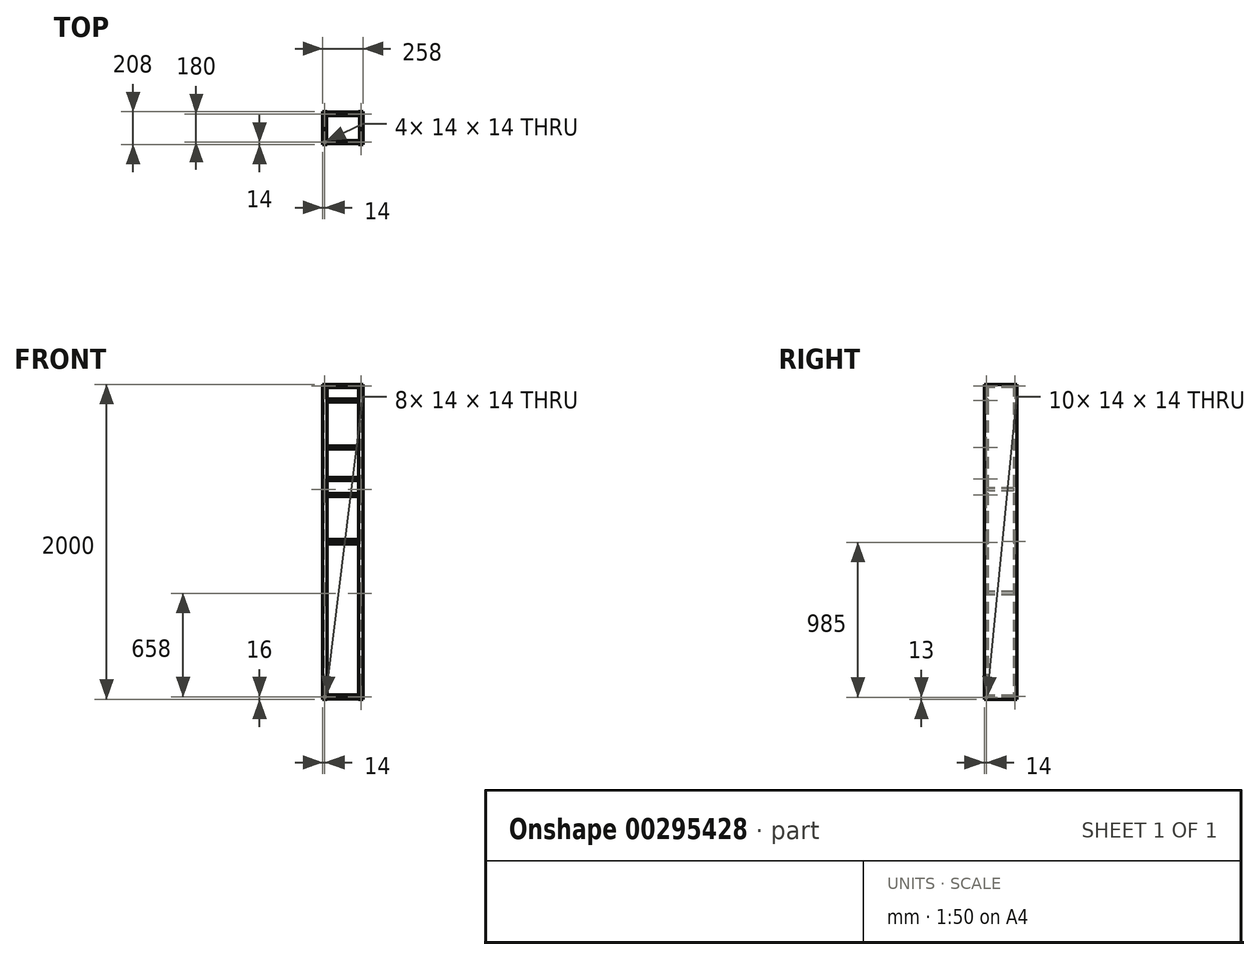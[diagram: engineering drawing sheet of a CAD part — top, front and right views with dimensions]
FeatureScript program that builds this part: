
annotation { "Feature Type Name" : "Feature", "Feature Type Description" : "" }
export const myFeature = defineFeature(function(context is Context, id is Id, definition is map)
    precondition{}
    {
        {
            var Q0;
            Q0=qCreatedBy(makeId("Top.planeOp"),FACE);
            var sketch = newSketch(context, id + "F0", { "sketchPlane" : qUnion([Q0])});
            skLineSegment(sketch, "E0", {"start": v(125, 0) * mm, "end": v(125, 100) * mm, "construction": true});
            skLineSegment(sketch, "E1", {"start": v(125, 100) * mm, "end": v(0, 100) * mm, "construction": true});
            skLineSegment(sketch, "E2.bottom", {"start": v(0, 0) * mm, "end": v(20, 0) * mm});
            skLineSegment(sketch, "E2.top", {"start": v(0, 20) * mm, "end": v(20, 20) * mm});
            skLineSegment(sketch, "E2.left", {"start": v(0, 0) * mm, "end": v(0, 20) * mm});
            skLineSegment(sketch, "E2.right", {"start": v(20, 0) * mm, "end": v(20, 20) * mm});
            skLineSegment(sketch, "E3.0", {"start": v(3, 17) * mm, "end": v(17, 17) * mm});
            skLineSegment(sketch, "E3.1", {"start": v(3, 3) * mm, "end": v(3, 17) * mm});
            skLineSegment(sketch, "E3.2", {"start": v(3, 3) * mm, "end": v(17, 3) * mm});
            skLineSegment(sketch, "E3.3", {"start": v(17, 3) * mm, "end": v(17, 17) * mm});
            skLineSegment(sketch, "E4.MirrorCS", {"start": v(250, 0) * mm, "end": v(230, 0) * mm});
            skLineSegment(sketch, "E5.MirrorCS", {"start": v(250, 20) * mm, "end": v(230, 20) * mm});
            skLineSegment(sketch, "E6.MirrorCS", {"start": v(250, 0) * mm, "end": v(250, 20) * mm});
            skLineSegment(sketch, "E7.MirrorCS", {"start": v(233, 3) * mm, "end": v(233, 17) * mm});
            skLineSegment(sketch, "E8.MirrorCS", {"start": v(247, 3) * mm, "end": v(233, 3) * mm});
            skLineSegment(sketch, "E9.MirrorCS", {"start": v(230, 0) * mm, "end": v(230, 20) * mm});
            skLineSegment(sketch, "E10.MirrorCS", {"start": v(247, 17) * mm, "end": v(233, 17) * mm});
            skLineSegment(sketch, "E11.MirrorCS", {"start": v(247, 3) * mm, "end": v(247, 17) * mm});
            skLineSegment(sketch, "E12.MirrorCS", {"start": v(247, 183) * mm, "end": v(233, 183) * mm});
            skLineSegment(sketch, "E13.MirrorCS", {"start": v(250, 200) * mm, "end": v(250, 180) * mm});
            skLineSegment(sketch, "E14.MirrorCS", {"start": v(250, 180) * mm, "end": v(230, 180) * mm});
            skLineSegment(sketch, "E15.MirrorCS", {"start": v(250, 200) * mm, "end": v(230, 200) * mm});
            skLineSegment(sketch, "E16.MirrorCS", {"start": v(17, 197) * mm, "end": v(17, 183) * mm});
            skLineSegment(sketch, "E17.MirrorCS", {"start": v(3, 197) * mm, "end": v(17, 197) * mm});
            skLineSegment(sketch, "E18.MirrorCS", {"start": v(3, 197) * mm, "end": v(3, 183) * mm});
            skLineSegment(sketch, "E19.MirrorCS", {"start": v(3, 183) * mm, "end": v(17, 183) * mm});
            skLineSegment(sketch, "E20.MirrorCS", {"start": v(20, 200) * mm, "end": v(20, 180) * mm});
            skLineSegment(sketch, "E21.MirrorCS", {"start": v(0, 200) * mm, "end": v(20, 200) * mm});
            skLineSegment(sketch, "E22.MirrorCS", {"start": v(0, 200) * mm, "end": v(0, 180) * mm});
            skLineSegment(sketch, "E23.MirrorCS", {"start": v(230, 200) * mm, "end": v(230, 180) * mm});
            skLineSegment(sketch, "E24.MirrorCS", {"start": v(0, 180) * mm, "end": v(20, 180) * mm});
            skLineSegment(sketch, "E25.MirrorCS", {"start": v(247, 197) * mm, "end": v(247, 183) * mm});
            skLineSegment(sketch, "E26.MirrorCS", {"start": v(247, 197) * mm, "end": v(233, 197) * mm});
            skLineSegment(sketch, "E27.MirrorCS", {"start": v(233, 197) * mm, "end": v(233, 183) * mm});
            skSolve(sketch);
        }
        {
            var Q0;
            Q0=makeQuery(id+"F0.imprint","IMPRINT",FACE,{"disambiguationData":[TD([[makeQuery(id+"F0.imprint","IMPRINT",EDGE,{"derivedFrom":sQuery(id+"F0.wireOp",EDGE,"E16.MirrorCS")}),1.0]])]});
            var Q1;
            Q1=makeQuery(id+"F0.imprint","IMPRINT",FACE,{"disambiguationData":[TD([[makeQuery(id+"F0.imprint","IMPRINT",EDGE,{"derivedFrom":sQuery(id+"F0.wireOp",EDGE,"E12.MirrorCS")}),1.0]])]});
            var Q2;
            Q2=makeQuery(id+"F0.imprint","IMPRINT",FACE,{"disambiguationData":[TD([[makeQuery(id+"F0.imprint","IMPRINT",EDGE,{"derivedFrom":sQuery(id+"F0.wireOp",EDGE,"E4.MirrorCS")}),-1.0]])]});
            var Q3;
            Q3=makeQuery(id+"F0.imprint","IMPRINT",FACE,{"disambiguationData":[TD([[makeQuery(id+"F0.imprint","IMPRINT",EDGE,{"derivedFrom":sQuery(id+"F0.wireOp",EDGE,"E2.bottom")}),1.0]])]});
            var Q4;
            Q4=makeQuery(id+"F0.imprint","IMPRINT",FACE,{"disambiguationData":[TD([[makeQuery(id+"F0.imprint","IMPRINT",EDGE,{"derivedFrom":sQuery(id+"F0.wireOp",EDGE,"1bdd15c0-c4f6-4624-8977-0df94d45482211.MirrorCS")}),1.0]])]});
            var Q5;
            Q5=makeQuery(id+"F0.imprint","IMPRINT",FACE,{"disambiguationData":[TD([[makeQuery(id+"F0.imprint","IMPRINT",EDGE,{"derivedFrom":sQuery(id+"F0.wireOp",EDGE,"1bdd15c0-c4f6-4624-8977-0df94d4548226.MirrorCS")}),-1.0]])]});
            extrude(context, id + "F1", {"entities" : qUnion([Q0, Q1, Q2, Q3, Q4, Q5]), "depth" : 2000 * mm});
        }
        {
            var Q0;
            Q0=qCreatedBy(makeId("Top.planeOp"),FACE);
            var sketch = newSketch(context, id + "F2", { "sketchPlane" : qUnion([Q0])});
            skLineSegment(sketch, "E28", {"start": v(0, 0) * mm, "end": v(0, 200.03) * mm});
            skLineSegment(sketch, "E29", {"start": v(125, 0) * mm, "end": v(125, 89.21) * mm, "construction": true});
            skLineSegment(sketch, "E30", {"start": v(0, 0) * mm, "end": v(20, 0) * mm});
            skLineSegment(sketch, "E31", {"start": v(20, 0) * mm, "end": v(20, 20) * mm});
            skLineSegment(sketch, "E32.0", {"start": v(24, -4) * mm, "end": v(24, 20) * mm});
            skLineSegment(sketch, "E32.2", {"start": v(-4, 204) * mm, "end": v(24, 204) * mm});
            skLineSegment(sketch, "E32.3", {"start": v(-4, -4) * mm, "end": v(-4, 204) * mm});
            skLineSegment(sketch, "E32.4", {"start": v(-4, -4) * mm, "end": v(24, -4) * mm});
            skLineSegment(sketch, "E33", {"start": v(24, 20) * mm, "end": v(20, 20) * mm});
            skLineSegment(sketch, "E34.MirrorCS", {"start": v(226, 20) * mm, "end": v(230, 20) * mm});
            skLineSegment(sketch, "E35.MirrorCS", {"start": v(250, 0) * mm, "end": v(250, 200) * mm});
            skLineSegment(sketch, "E36.MirrorCS", {"start": v(254, -4) * mm, "end": v(226, -4) * mm});
            skLineSegment(sketch, "E37.MirrorCS", {"start": v(254, 204) * mm, "end": v(226, 204) * mm});
            skLineSegment(sketch, "E38.MirrorCS", {"start": v(226, -4) * mm, "end": v(226, 20) * mm});
            skLineSegment(sketch, "E39.MirrorCS", {"start": v(230, 0) * mm, "end": v(230, 20) * mm});
            skLineSegment(sketch, "E40.MirrorCS", {"start": v(254, -4) * mm, "end": v(254, 204) * mm});
            skLineSegment(sketch, "E41.MirrorCS", {"start": v(250, 0) * mm, "end": v(230, 0) * mm});
            skLineSegment(sketch, "E42", {"start": v(0, 200.03) * mm, "end": v(20.11, 200.03) * mm});
            skLineSegment(sketch, "E43", {"start": v(20.11, 200.03) * mm, "end": v(20.11, 179.96) * mm});
            skLineSegment(sketch, "E44", {"start": v(20.11, 179.96) * mm, "end": v(24.11, 179.96) * mm});
            skLineSegment(sketch, "E45", {"start": v(24, 204) * mm, "end": v(24.11, 179.96) * mm});
            skLineSegment(sketch, "E46", {"start": v(249.91, 204) * mm, "end": v(226, 204) * mm});
            skLineSegment(sketch, "E47", {"start": v(250, 200) * mm, "end": v(230, 200) * mm});
            skLineSegment(sketch, "E48", {"start": v(230, 179.84) * mm, "end": v(230, 200) * mm});
            skLineSegment(sketch, "E49", {"start": v(230, 179.84) * mm, "end": v(226, 179.84) * mm});
            skLineSegment(sketch, "E50", {"start": v(226, 204) * mm, "end": v(226, 179.84) * mm});
            skSolve(sketch);
        }
        {
            var Q0;
            Q0 = qSketchRegion(id + "F2", true);
            extrude(context, id + "F3", {"entities" : qUnion([Q0]), "depth" : 2000 * mm});
        }
        {
            var Q0;
            Q0=makeQuery(id+"F1.opExtrude","SWEPT_FACE",FACE,{"disambiguationData":[OSD([sQuery(id+"F0.wireOp",EDGE,"E2.right")])]});
            var sketch = newSketch(context, id + "F4", { "sketchPlane" : qUnion([Q0])});
            skLineSegment(sketch, "E51.bottom", {"start": v(20, 2000) * mm, "end": v(0, 2000) * mm});
            skLineSegment(sketch, "E51.top", {"start": v(20, 1980) * mm, "end": v(0, 1980) * mm});
            skLineSegment(sketch, "E51.left", {"start": v(20, 2000) * mm, "end": v(20, 1980) * mm});
            skLineSegment(sketch, "E51.right", {"start": v(0, 2000) * mm, "end": v(0, 1980) * mm});
            skLineSegment(sketch, "E52.0", {"start": v(17, 1983) * mm, "end": v(3, 1983) * mm});
            skLineSegment(sketch, "E52.1", {"start": v(17, 1997) * mm, "end": v(17, 1983) * mm});
            skLineSegment(sketch, "E52.2", {"start": v(17, 1997) * mm, "end": v(3, 1997) * mm});
            skLineSegment(sketch, "E52.3", {"start": v(3, 1997) * mm, "end": v(3, 1983) * mm});
            skLineSegment(sketch, "E53.0.1.1", {"start": v(0, 1909) * mm, "end": v(0, 1889) * mm});
            skLineSegment(sketch, "E53.0.1.2", {"start": v(17, 1906) * mm, "end": v(3, 1906) * mm});
            skLineSegment(sketch, "E53.0.1.4", {"start": v(20, 1909) * mm, "end": v(0, 1909) * mm});
            skLineSegment(sketch, "E53.0.1.5", {"start": v(17, 1892) * mm, "end": v(3, 1892) * mm});
            skLineSegment(sketch, "E53.0.1.6", {"start": v(17, 1906) * mm, "end": v(17, 1892) * mm});
            skLineSegment(sketch, "E53.0.1.7", {"start": v(3, 1906) * mm, "end": v(3, 1892) * mm});
            skLineSegment(sketch, "E53.0.1.8", {"start": v(20, 1909) * mm, "end": v(20, 1889) * mm});
            skLineSegment(sketch, "E53.0.1.9", {"start": v(20, 1889) * mm, "end": v(0, 1889) * mm});
            skLineSegment(sketch, "E54.0.1.0", {"start": v(20, 1609) * mm, "end": v(20, 1589) * mm});
            skLineSegment(sketch, "E54.0.1.1", {"start": v(17, 1606) * mm, "end": v(3, 1606) * mm});
            skLineSegment(sketch, "E54.0.1.2", {"start": v(20, 1589) * mm, "end": v(0, 1589) * mm});
            skLineSegment(sketch, "E54.0.1.3", {"start": v(17, 1606) * mm, "end": v(17, 1592) * mm});
            skLineSegment(sketch, "E54.0.1.4", {"start": v(0, 1609) * mm, "end": v(0, 1589) * mm});
            skLineSegment(sketch, "E54.0.1.5", {"start": v(17, 1592) * mm, "end": v(3, 1592) * mm});
            skLineSegment(sketch, "E54.0.1.6", {"start": v(3, 1606) * mm, "end": v(3, 1592) * mm});
            skLineSegment(sketch, "E54.0.1.7", {"start": v(20, 1609) * mm, "end": v(0, 1609) * mm});
            skLineSegment(sketch, "E55.0.1.0", {"start": v(20, 1409) * mm, "end": v(20, 1389) * mm});
            skLineSegment(sketch, "E55.0.1.1", {"start": v(3, 1406) * mm, "end": v(3, 1392) * mm});
            skLineSegment(sketch, "E55.0.1.2", {"start": v(17, 1406) * mm, "end": v(17, 1392) * mm});
            skLineSegment(sketch, "E55.0.1.3", {"start": v(0, 1409) * mm, "end": v(0, 1389) * mm});
            skLineSegment(sketch, "E55.0.1.4", {"start": v(20, 1409) * mm, "end": v(0, 1409) * mm});
            skLineSegment(sketch, "E55.0.1.5", {"start": v(20, 1389) * mm, "end": v(0, 1389) * mm});
            skLineSegment(sketch, "E55.0.1.6", {"start": v(17, 1406) * mm, "end": v(3, 1406) * mm});
            skLineSegment(sketch, "E55.0.1.7", {"start": v(17, 1392) * mm, "end": v(3, 1392) * mm});
            skLineSegment(sketch, "E56.0.1.0", {"start": v(17, 1305) * mm, "end": v(17, 1291) * mm});
            skLineSegment(sketch, "E56.0.1.1", {"start": v(20, 1308) * mm, "end": v(0, 1308) * mm});
            skLineSegment(sketch, "E56.0.1.2", {"start": v(3, 1305) * mm, "end": v(3, 1291) * mm});
            skLineSegment(sketch, "E56.0.1.3", {"start": v(20, 1308) * mm, "end": v(20, 1288) * mm});
            skLineSegment(sketch, "E56.0.1.4", {"start": v(20, 1288) * mm, "end": v(0, 1288) * mm});
            skLineSegment(sketch, "E56.0.1.5", {"start": v(0, 1308) * mm, "end": v(0, 1288) * mm});
            skLineSegment(sketch, "E56.0.1.6", {"start": v(17, 1291) * mm, "end": v(3, 1291) * mm});
            skLineSegment(sketch, "E56.0.1.7", {"start": v(17, 1305) * mm, "end": v(3, 1305) * mm});
            skLineSegment(sketch, "E57.0.1.0", {"start": v(20, 1008) * mm, "end": v(20, 988) * mm});
            skLineSegment(sketch, "E57.0.1.1", {"start": v(0, 1008) * mm, "end": v(0, 988) * mm});
            skLineSegment(sketch, "E57.0.1.2", {"start": v(20, 988) * mm, "end": v(0, 988) * mm});
            skLineSegment(sketch, "E57.0.1.3", {"start": v(3, 1005) * mm, "end": v(3, 991) * mm});
            skLineSegment(sketch, "E57.0.1.4", {"start": v(20, 1008) * mm, "end": v(0, 1008) * mm});
            skLineSegment(sketch, "E57.0.1.5", {"start": v(17, 1005) * mm, "end": v(17, 991) * mm});
            skLineSegment(sketch, "E57.0.1.6", {"start": v(17, 991) * mm, "end": v(3, 991) * mm});
            skLineSegment(sketch, "E57.0.1.7", {"start": v(17, 1005) * mm, "end": v(3, 1005) * mm});
            skLineSegment(sketch, "E58.0.1.0", {"start": v(17, 20) * mm, "end": v(17, 6) * mm});
            skLineSegment(sketch, "E58.0.1.1", {"start": v(3, 20) * mm, "end": v(3, 6) * mm});
            skLineSegment(sketch, "E58.0.1.2", {"start": v(17, 6) * mm, "end": v(3, 6) * mm});
            skLineSegment(sketch, "E58.0.1.3", {"start": v(0, 23) * mm, "end": v(0, 3) * mm});
            skLineSegment(sketch, "E58.0.1.4", {"start": v(20, 3) * mm, "end": v(0, 3) * mm});
            skLineSegment(sketch, "E58.0.1.5", {"start": v(20, 23) * mm, "end": v(20, 3) * mm});
            skLineSegment(sketch, "E58.0.1.6", {"start": v(20, 23) * mm, "end": v(0, 23) * mm});
            skLineSegment(sketch, "E58.0.1.7", {"start": v(17, 20) * mm, "end": v(3, 20) * mm});
            skSolve(sketch);
        }
        {
            var Q0;
            Q0 = qSketchRegion(id + "F4", true);
            extrude(context, id + "F5", {"entities" : qUnion([Q0]), "depth" : 210 * mm});
        }
        {
            var Q0;
            Q0=makeQuery(id+"F1.opExtrude","SWEPT_FACE",FACE,{"disambiguationData":[OSD([sQuery(id+"F0.wireOp",EDGE,"E2.top")])]});
            var sketch = newSketch(context, id + "F6", { "sketchPlane" : qUnion([Q0])});
            skLineSegment(sketch, "E59.bottom", {"start": v(-20, 2000) * mm, "end": v(0, 2000) * mm});
            skLineSegment(sketch, "E59.top", {"start": v(-20, 1980) * mm, "end": v(0, 1980) * mm});
            skLineSegment(sketch, "E59.left", {"start": v(-20, 2000) * mm, "end": v(-20, 1980) * mm});
            skLineSegment(sketch, "E59.right", {"start": v(0, 2000) * mm, "end": v(0, 1980) * mm});
            skLineSegment(sketch, "E60.0", {"start": v(-17, 1997) * mm, "end": v(-17, 1983) * mm});
            skLineSegment(sketch, "E60.1", {"start": v(-17, 1997) * mm, "end": v(-3, 1997) * mm});
            skLineSegment(sketch, "E60.2", {"start": v(-3, 1997) * mm, "end": v(-3, 1983) * mm});
            skLineSegment(sketch, "E60.3", {"start": v(-17, 1983) * mm, "end": v(-3, 1983) * mm});
            skPoint(sketch, "E61.endSnap0", {"position": v(-17, 1990) * mm});
            skLineSegment(sketch, "E62.MirrorCS", {"start": v(-250, 2000) * mm, "end": v(-250, 1980) * mm});
            skLineSegment(sketch, "E63.MirrorCS", {"start": v(-233, 1997) * mm, "end": v(-233, 1983) * mm});
            skLineSegment(sketch, "E64.MirrorCS", {"start": v(-230, 1980) * mm, "end": v(-250, 1980) * mm});
            skLineSegment(sketch, "E65.MirrorCS", {"start": v(-233, 1983) * mm, "end": v(-247, 1983) * mm});
            skLineSegment(sketch, "E66.MirrorCS", {"start": v(-230, 2000) * mm, "end": v(-250, 2000) * mm});
            skPoint(sketch, "E67.MirrorP", {"position": v(-233, 1990) * mm});
            skLineSegment(sketch, "E68.MirrorCS", {"start": v(-233, 1997) * mm, "end": v(-247, 1997) * mm});
            skLineSegment(sketch, "E69.MirrorCS", {"start": v(-247, 1997) * mm, "end": v(-247, 1983) * mm});
            skLineSegment(sketch, "E70.MirrorCS", {"start": v(-230, 2000) * mm, "end": v(-230, 1980) * mm});
            skPoint(sketch, "E71.0.1.0", {"position": v(-17, 1332) * mm});
            skPoint(sketch, "E71.0.1.1", {"position": v(-233, 1332) * mm});
            skLineSegment(sketch, "E71.0.1.2", {"start": v(0, 1342) * mm, "end": v(0, 1322) * mm});
            skLineSegment(sketch, "E71.0.1.3", {"start": v(-17, 1339) * mm, "end": v(-17, 1325) * mm});
            skLineSegment(sketch, "E71.0.1.4", {"start": v(-20, 1322) * mm, "end": v(0, 1322) * mm});
            skLineSegment(sketch, "E71.0.1.5", {"start": v(-230, 1322) * mm, "end": v(-250, 1322) * mm});
            skLineSegment(sketch, "E71.0.1.6", {"start": v(-233, 1325) * mm, "end": v(-247, 1325) * mm});
            skLineSegment(sketch, "E71.0.1.7", {"start": v(-250, 1342) * mm, "end": v(-250, 1322) * mm});
            skLineSegment(sketch, "E71.0.1.8", {"start": v(-230, 1342) * mm, "end": v(-250, 1342) * mm});
            skLineSegment(sketch, "E71.0.1.9", {"start": v(-17, 1325) * mm, "end": v(-3, 1325) * mm});
            skLineSegment(sketch, "E71.0.1.10", {"start": v(-233, 1339) * mm, "end": v(-233, 1325) * mm});
            skLineSegment(sketch, "E71.0.1.11", {"start": v(-3, 1339) * mm, "end": v(-3, 1325) * mm});
            skLineSegment(sketch, "E71.0.1.12", {"start": v(-17, 1339) * mm, "end": v(-3, 1339) * mm});
            skLineSegment(sketch, "E71.0.1.13", {"start": v(-20, 1342) * mm, "end": v(-20, 1322) * mm});
            skLineSegment(sketch, "E71.0.1.14", {"start": v(-20, 1342) * mm, "end": v(0, 1342) * mm});
            skLineSegment(sketch, "E71.0.1.15", {"start": v(-230, 1342) * mm, "end": v(-230, 1322) * mm});
            skLineSegment(sketch, "E71.0.1.16", {"start": v(-247, 1339) * mm, "end": v(-247, 1325) * mm});
            skLineSegment(sketch, "E71.0.1.17", {"start": v(-233, 1339) * mm, "end": v(-247, 1339) * mm});
            skPoint(sketch, "E71.0.2.0", {"position": v(-17, 674) * mm});
            skPoint(sketch, "E71.0.2.1", {"position": v(-233, 674) * mm});
            skLineSegment(sketch, "E71.0.2.2", {"start": v(0, 684) * mm, "end": v(0, 664) * mm});
            skLineSegment(sketch, "E71.0.2.3", {"start": v(-17, 681) * mm, "end": v(-17, 667) * mm});
            skLineSegment(sketch, "E71.0.2.4", {"start": v(-20, 664) * mm, "end": v(0, 664) * mm});
            skLineSegment(sketch, "E71.0.2.5", {"start": v(-230, 664) * mm, "end": v(-250, 664) * mm});
            skLineSegment(sketch, "E71.0.2.6", {"start": v(-233, 667) * mm, "end": v(-247, 667) * mm});
            skLineSegment(sketch, "E71.0.2.7", {"start": v(-250, 684) * mm, "end": v(-250, 664) * mm});
            skLineSegment(sketch, "E71.0.2.8", {"start": v(-230, 684) * mm, "end": v(-250, 684) * mm});
            skLineSegment(sketch, "E71.0.2.9", {"start": v(-17, 667) * mm, "end": v(-3, 667) * mm});
            skLineSegment(sketch, "E71.0.2.10", {"start": v(-233, 681) * mm, "end": v(-233, 667) * mm});
            skLineSegment(sketch, "E71.0.2.11", {"start": v(-3, 681) * mm, "end": v(-3, 667) * mm});
            skLineSegment(sketch, "E71.0.2.12", {"start": v(-17, 681) * mm, "end": v(-3, 681) * mm});
            skLineSegment(sketch, "E71.0.2.13", {"start": v(-20, 684) * mm, "end": v(-20, 664) * mm});
            skLineSegment(sketch, "E71.0.2.14", {"start": v(-20, 684) * mm, "end": v(0, 684) * mm});
            skLineSegment(sketch, "E71.0.2.15", {"start": v(-230, 684) * mm, "end": v(-230, 664) * mm});
            skLineSegment(sketch, "E71.0.2.16", {"start": v(-247, 681) * mm, "end": v(-247, 667) * mm});
            skLineSegment(sketch, "E71.0.2.17", {"start": v(-233, 681) * mm, "end": v(-247, 681) * mm});
            skPoint(sketch, "E71.0.3.0", {"position": v(-17, 16) * mm});
            skPoint(sketch, "E71.0.3.1", {"position": v(-233, 16) * mm});
            skLineSegment(sketch, "E71.0.3.2", {"start": v(0, 26) * mm, "end": v(0, 6) * mm});
            skLineSegment(sketch, "E71.0.3.3", {"start": v(-17, 23) * mm, "end": v(-17, 9) * mm});
            skLineSegment(sketch, "E71.0.3.4", {"start": v(-20, 6) * mm, "end": v(0, 6) * mm});
            skLineSegment(sketch, "E71.0.3.5", {"start": v(-230, 6) * mm, "end": v(-250, 6) * mm});
            skLineSegment(sketch, "E71.0.3.6", {"start": v(-233, 9) * mm, "end": v(-247, 9) * mm});
            skLineSegment(sketch, "E71.0.3.7", {"start": v(-250, 26) * mm, "end": v(-250, 6) * mm});
            skLineSegment(sketch, "E71.0.3.8", {"start": v(-230, 26) * mm, "end": v(-250, 26) * mm});
            skLineSegment(sketch, "E71.0.3.9", {"start": v(-17, 9) * mm, "end": v(-3, 9) * mm});
            skLineSegment(sketch, "E71.0.3.10", {"start": v(-233, 23) * mm, "end": v(-233, 9) * mm});
            skLineSegment(sketch, "E71.0.3.11", {"start": v(-3, 23) * mm, "end": v(-3, 9) * mm});
            skLineSegment(sketch, "E71.0.3.12", {"start": v(-17, 23) * mm, "end": v(-3, 23) * mm});
            skLineSegment(sketch, "E71.0.3.13", {"start": v(-20, 26) * mm, "end": v(-20, 6) * mm});
            skLineSegment(sketch, "E71.0.3.14", {"start": v(-20, 26) * mm, "end": v(0, 26) * mm});
            skLineSegment(sketch, "E71.0.3.15", {"start": v(-230, 26) * mm, "end": v(-230, 6) * mm});
            skLineSegment(sketch, "E71.0.3.16", {"start": v(-247, 23) * mm, "end": v(-247, 9) * mm});
            skLineSegment(sketch, "E71.0.3.17", {"start": v(-233, 23) * mm, "end": v(-247, 23) * mm});
            skLineSegment(sketch, "E71.direction1", {"start": v(-250, 1980) * mm, "end": v(-225, 1980) * mm, "construction": true});
            skLineSegment(sketch, "E71.direction2", {"start": v(-250, 1980) * mm, "end": v(-250, 1322) * mm, "construction": true});
            skSolve(sketch);
        }
        {
            var Q0;
            Q0 = qSketchRegion(id + "F6", true);
            extrude(context, id + "F7", {"entities" : qUnion([Q0]), "depth" : 160 * mm});
        }
        {
            var Q0;
            Q0=makeQuery(id+"F1.opExtrude","SWEPT_FACE",FACE,{"disambiguationData":[OSD([sQuery(id+"F0.wireOp",EDGE,"E20.MirrorCS")])]});
            var sketch = newSketch(context, id + "F8", { "sketchPlane" : qUnion([Q0])});
            skLineSegment(sketch, "E72.bottom", {"start": v(180, 2000) * mm, "end": v(200, 2000) * mm});
            skLineSegment(sketch, "E72.top", {"start": v(180, 1980) * mm, "end": v(200, 1980) * mm});
            skLineSegment(sketch, "E72.left", {"start": v(180, 2000) * mm, "end": v(180, 1980) * mm});
            skLineSegment(sketch, "E72.right", {"start": v(200, 2000) * mm, "end": v(200, 1980) * mm});
            skLineSegment(sketch, "E73.0", {"start": v(183, 1997) * mm, "end": v(197, 1997) * mm});
            skLineSegment(sketch, "E73.1", {"start": v(183, 1997) * mm, "end": v(183, 1983) * mm});
            skLineSegment(sketch, "E73.2", {"start": v(183, 1983) * mm, "end": v(197, 1983) * mm});
            skLineSegment(sketch, "E73.3", {"start": v(197, 1997) * mm, "end": v(197, 1983) * mm});
            skLineSegment(sketch, "E74.0.1.0", {"start": v(183, 997) * mm, "end": v(197, 997) * mm});
            skLineSegment(sketch, "E74.0.1.1", {"start": v(180, 1014) * mm, "end": v(180, 994) * mm});
            skLineSegment(sketch, "E74.0.1.2", {"start": v(197, 1011) * mm, "end": v(197, 997) * mm});
            skLineSegment(sketch, "E74.0.1.3", {"start": v(180, 994) * mm, "end": v(200, 994) * mm});
            skLineSegment(sketch, "E74.0.1.4", {"start": v(183, 1011) * mm, "end": v(183, 997) * mm});
            skLineSegment(sketch, "E74.0.1.5", {"start": v(180, 1014) * mm, "end": v(200, 1014) * mm});
            skLineSegment(sketch, "E74.0.1.6", {"start": v(183, 1011) * mm, "end": v(197, 1011) * mm});
            skLineSegment(sketch, "E74.0.1.7", {"start": v(200, 1014) * mm, "end": v(200, 994) * mm});
            skLineSegment(sketch, "E74.0.2.0", {"start": v(183, 11) * mm, "end": v(197, 11) * mm});
            skLineSegment(sketch, "E74.0.2.1", {"start": v(180, 28) * mm, "end": v(180, 8) * mm});
            skLineSegment(sketch, "E74.0.2.2", {"start": v(197, 25) * mm, "end": v(197, 11) * mm});
            skLineSegment(sketch, "E74.0.2.3", {"start": v(180, 8) * mm, "end": v(200, 8) * mm});
            skLineSegment(sketch, "E74.0.2.4", {"start": v(183, 25) * mm, "end": v(183, 11) * mm});
            skLineSegment(sketch, "E74.0.2.5", {"start": v(180, 28) * mm, "end": v(200, 28) * mm});
            skLineSegment(sketch, "E74.0.2.6", {"start": v(183, 25) * mm, "end": v(197, 25) * mm});
            skLineSegment(sketch, "E74.0.2.7", {"start": v(200, 28) * mm, "end": v(200, 8) * mm});
            skLineSegment(sketch, "E74.direction1", {"start": v(180, 1980) * mm, "end": v(205, 1980) * mm, "construction": true});
            skLineSegment(sketch, "E74.direction2", {"start": v(180, 1980) * mm, "end": v(180, 994) * mm, "construction": true});
            skSolve(sketch);
        }
        {
            var Q0;
            Q0 = qSketchRegion(id + "F8", true);
            extrude(context, id + "F9", {"entities" : qUnion([Q0]), "depth" : 210 * mm});
        }
    });
